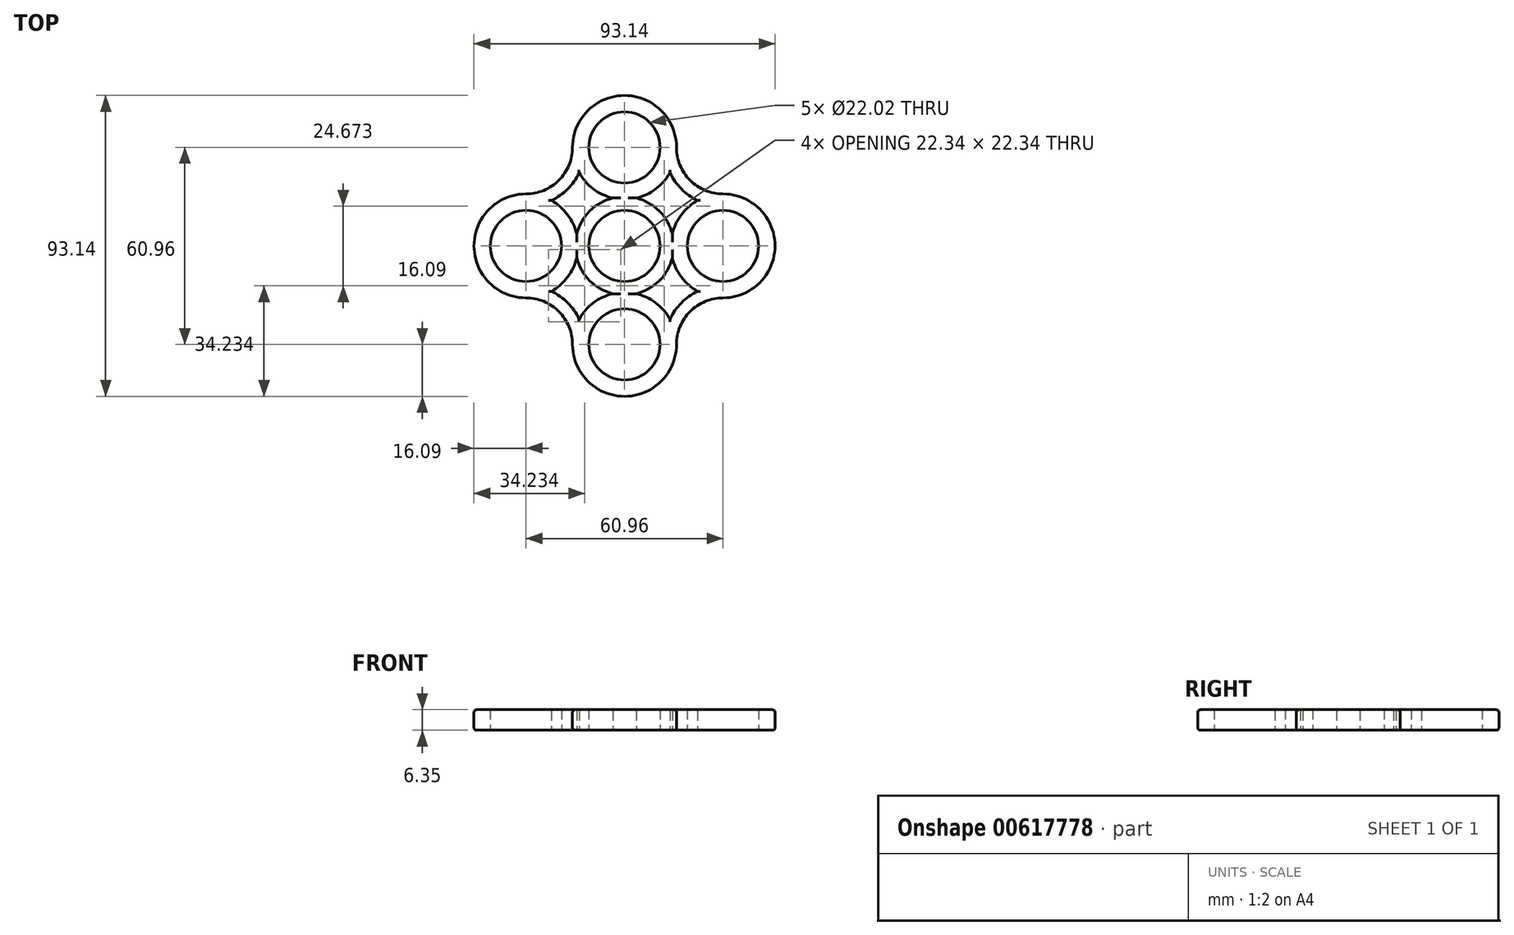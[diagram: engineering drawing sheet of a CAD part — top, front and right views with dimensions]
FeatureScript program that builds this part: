
annotation { "Feature Type Name" : "Feature", "Feature Type Description" : "" }
export const myFeature = defineFeature(function(context is Context, id is Id, definition is map)
    precondition{}
    {
        {
            var Q0;
            Q0=qCreatedBy(makeId("Top.planeOp"),FACE);
            var sketch = newSketch(context, id + "F0", { "sketchPlane" : qUnion([Q0])});
            skCircle(sketch, "E0", {"center": v(0, 0) * mm, "radius": 11.01 * mm});
            skLineSegment(sketch, "E1", {"start": v(0, 0) * mm, "end": v(-30.48, 0) * mm});
            skLineSegment(sketch, "E2", {"start": v(0, 0) * mm, "end": v(0, -30.48) * mm});
            skLineSegment(sketch, "E3", {"start": v(0, 0) * mm, "end": v(30.48, 0) * mm});
            skLineSegment(sketch, "E4", {"start": v(0, 0) * mm, "end": v(0, 30.48) * mm});
            skCircle(sketch, "E5", {"center": v(30.48, 0) * mm, "radius": 11.01 * mm});
            skCircle(sketch, "E6", {"center": v(-30.48, 0) * mm, "radius": 11.01 * mm});
            skCircle(sketch, "E7", {"center": v(0, 30.48) * mm, "radius": 11.01 * mm});
            skCircle(sketch, "E8", {"center": v(0, -30.48) * mm, "radius": 11.01 * mm});
            skCircle(sketch, "E9", {"center": v(-30.48, 0) * mm, "radius": 16.1 * mm});
            skCircle(sketch, "E10", {"center": v(0, 30.48) * mm, "radius": 16.1 * mm});
            skCircle(sketch, "E11", {"center": v(30.48, 0) * mm, "radius": 16.1 * mm});
            skCircle(sketch, "E12", {"center": v(0, -30.48) * mm, "radius": 16.1 * mm});
            skArc(sketch, "E13", {"start": v(-30.47, 16.1) * mm, "mid": v(-20.3, 20.3) * mm, "end": v(-16.1, 30.47) * mm});
            skArc(sketch, "E14", {"start": v(-16.1, -30.47) * mm, "mid": v(-20.3, -20.3) * mm, "end": v(-30.47, -16.1) * mm});
            skArc(sketch, "E15", {"start": v(30.47, -16.1) * mm, "mid": v(20.3, -20.3) * mm, "end": v(16.1, -30.47) * mm});
            skArc(sketch, "E16", {"start": v(16.1, 30.47) * mm, "mid": v(20.3, 20.3) * mm, "end": v(30.47, 16.1) * mm});
            skArc(sketch, "E17", {"start": v(-14.05, 22.64) * mm, "mid": v(-17.6, 17.6) * mm, "end": v(-22.64, 14.05) * mm});
            skArc(sketch, "E18", {"start": v(14.05, 22.64) * mm, "mid": v(17.6, 17.6) * mm, "end": v(22.64, 14.05) * mm});
            skArc(sketch, "E19", {"start": v(-22.64, -14.05) * mm, "mid": v(-17.6, -17.6) * mm, "end": v(-14.05, -22.64) * mm});
            skArc(sketch, "E20", {"start": v(14.05, -22.64) * mm, "mid": v(17.6, -17.6) * mm, "end": v(22.64, -14.05) * mm});
            skCircle(sketch, "E21", {"center": v(0, 0) * mm, "radius": 15.24 * mm});
            skSolve(sketch);
        }
        {
            var Q0;
            Q0 = qSketchRegion(id + "F0", true);
            var Q1;
            {var subQ0=sQuery(id+"F0.wireOp",EDGE,"E1");var subQ1=sQuery(id+"F0.wireOp",EDGE,"E0");var subQ2=makeQuery(id+"F0.imprint","INTERSECT",VERTEX,{"derivedFrom":[subQ1,subQ0]});Q1=makeQuery(id+"F0.imprint","IMPRINT",FACE,{"disambiguationData":[TD([[makeQuery(id+"F0.imprint","IMPRINT",EDGE,{"disambiguationData":[TD([[subQ2,-1.0]])],"derivedFrom":subQ1}),-1.0]])]});}
            var Q2;
            {var subQ0=sQuery(id+"F0.wireOp",EDGE,"E4");var subQ1=sQuery(id+"F0.wireOp",EDGE,"E0");var subQ2=makeQuery(id+"F0.imprint","INTERSECT",VERTEX,{"derivedFrom":[subQ1,subQ0]});Q2=makeQuery(id+"F0.imprint","IMPRINT",FACE,{"disambiguationData":[TD([[makeQuery(id+"F0.imprint","IMPRINT",EDGE,{"disambiguationData":[TD([[subQ2,-1.0]])],"derivedFrom":subQ1}),-1.0]])]});}
            var Q3;
            {var subQ0=sQuery(id+"F0.wireOp",EDGE,"E4");var subQ1=sQuery(id+"F0.wireOp",EDGE,"E0");var subQ2=makeQuery(id+"F0.imprint","INTERSECT",VERTEX,{"derivedFrom":[subQ1,subQ0]});Q3=makeQuery(id+"F0.imprint","IMPRINT",FACE,{"disambiguationData":[TD([[makeQuery(id+"F0.imprint","IMPRINT",EDGE,{"disambiguationData":[TD([[subQ2,1.0]])],"derivedFrom":subQ1}),-1.0]])]});}
            var Q4;
            {var subQ0=sQuery(id+"F0.wireOp",EDGE,"E3");var subQ1=sQuery(id+"F0.wireOp",EDGE,"E0");var subQ2=makeQuery(id+"F0.imprint","INTERSECT",VERTEX,{"derivedFrom":[subQ1,subQ0]});Q4=makeQuery(id+"F0.imprint","IMPRINT",FACE,{"disambiguationData":[TD([[makeQuery(id+"F0.imprint","IMPRINT",EDGE,{"disambiguationData":[TD([[subQ2,1.0]])],"derivedFrom":subQ1}),-1.0]])]});}
            var Q5;
            {var subQ0=sQuery(id+"F0.wireOp",EDGE,"E21");var subQ1=sQuery(id+"F0.wireOp",EDGE,"E1");var subQ2=makeQuery(id+"F0.imprint","INTERSECT",VERTEX,{"derivedFrom":[subQ1,subQ0]});Q5=makeQuery(id+"F0.imprint","IMPRINT",FACE,{"disambiguationData":[TD([[makeQuery(id+"F0.imprint","IMPRINT",EDGE,{"disambiguationData":[TD([[subQ2,1.0]])],"derivedFrom":subQ1}),-1.0]])]});}
            var Q6;
            {var subQ0=sQuery(id+"F0.wireOp",EDGE,"E21");var subQ1=sQuery(id+"F0.wireOp",EDGE,"E1");var subQ2=makeQuery(id+"F0.imprint","INTERSECT",VERTEX,{"derivedFrom":[subQ1,subQ0]});Q6=makeQuery(id+"F0.imprint","IMPRINT",FACE,{"disambiguationData":[TD([[makeQuery(id+"F0.imprint","IMPRINT",EDGE,{"disambiguationData":[TD([[subQ2,1.0]])],"derivedFrom":subQ1}),1.0]])]});}
            var Q7;
            {var subQ0=sQuery(id+"F0.wireOp",EDGE,"E21");var subQ1=sQuery(id+"F0.wireOp",EDGE,"E4");var subQ2=makeQuery(id+"F0.imprint","INTERSECT",VERTEX,{"derivedFrom":[subQ1,subQ0]});Q7=makeQuery(id+"F0.imprint","IMPRINT",FACE,{"disambiguationData":[TD([[makeQuery(id+"F0.imprint","IMPRINT",EDGE,{"disambiguationData":[TD([[subQ2,1.0]])],"derivedFrom":subQ1}),1.0]])]});}
            var Q8;
            {var subQ0=sQuery(id+"F0.wireOp",EDGE,"E21");var subQ1=sQuery(id+"F0.wireOp",EDGE,"E4");var subQ2=makeQuery(id+"F0.imprint","INTERSECT",VERTEX,{"derivedFrom":[subQ1,subQ0]});Q8=makeQuery(id+"F0.imprint","IMPRINT",FACE,{"disambiguationData":[TD([[makeQuery(id+"F0.imprint","IMPRINT",EDGE,{"disambiguationData":[TD([[subQ2,1.0]])],"derivedFrom":subQ1}),-1.0]])]});}
            var Q9;
            {var subQ0=sQuery(id+"F0.wireOp",EDGE,"E21");var subQ1=sQuery(id+"F0.wireOp",EDGE,"E3");var subQ2=makeQuery(id+"F0.imprint","INTERSECT",VERTEX,{"derivedFrom":[subQ1,subQ0]});Q9=makeQuery(id+"F0.imprint","IMPRINT",FACE,{"disambiguationData":[TD([[makeQuery(id+"F0.imprint","IMPRINT",EDGE,{"disambiguationData":[TD([[subQ2,1.0]])],"derivedFrom":subQ1}),1.0]])]});}
            var Q10;
            {var subQ0=sQuery(id+"F0.wireOp",EDGE,"E21");var subQ1=sQuery(id+"F0.wireOp",EDGE,"E3");var subQ2=makeQuery(id+"F0.imprint","INTERSECT",VERTEX,{"derivedFrom":[subQ1,subQ0]});Q10=makeQuery(id+"F0.imprint","IMPRINT",FACE,{"disambiguationData":[TD([[makeQuery(id+"F0.imprint","IMPRINT",EDGE,{"disambiguationData":[TD([[subQ2,1.0]])],"derivedFrom":subQ1}),-1.0]])]});}
            var Q11;
            {var subQ0=sQuery(id+"F0.wireOp",EDGE,"E21");var subQ1=sQuery(id+"F0.wireOp",EDGE,"E2");var subQ2=makeQuery(id+"F0.imprint","INTERSECT",VERTEX,{"derivedFrom":[subQ1,subQ0]});Q11=makeQuery(id+"F0.imprint","IMPRINT",FACE,{"disambiguationData":[TD([[makeQuery(id+"F0.imprint","IMPRINT",EDGE,{"disambiguationData":[TD([[subQ2,1.0]])],"derivedFrom":subQ1}),1.0]])]});}
            var Q12;
            {var subQ0=sQuery(id+"F0.wireOp",EDGE,"E21");var subQ1=sQuery(id+"F0.wireOp",EDGE,"E2");var subQ2=makeQuery(id+"F0.imprint","INTERSECT",VERTEX,{"derivedFrom":[subQ1,subQ0]});Q12=makeQuery(id+"F0.imprint","IMPRINT",FACE,{"disambiguationData":[TD([[makeQuery(id+"F0.imprint","IMPRINT",EDGE,{"disambiguationData":[TD([[subQ2,1.0]])],"derivedFrom":subQ1}),-1.0]])]});}
            var Q13;
            {var subQ0=sQuery(id+"F0.wireOp",EDGE,"ufLXqPXd-shLM-E6S0-tGkO-5ok8c0KJ1qn1");Q13=makeQuery(id+"F0.imprint","IMPRINT",FACE,{"disambiguationData":[TD([[makeQuery(id+"F0.imprint","IMPRINT",EDGE,{"derivedFrom":subQ0}),-1.0]])]});}
            var Q14;
            {var subQ0=sQuery(id+"F0.wireOp",EDGE,"inb3N0IN-n71V-Iyvo-hvQc-OrFp1SuvMqcb");Q14=makeQuery(id+"F0.imprint","IMPRINT",FACE,{"disambiguationData":[TD([[makeQuery(id+"F0.imprint","IMPRINT",EDGE,{"derivedFrom":subQ0}),-1.0]])]});}
            extrude(context, id + "F1", {"entities" : qUnion([Q0, Q1, Q2, Q3, Q4, Q5, Q6, Q7, Q8, Q9, Q10, Q11, Q12, Q13, Q14]), "depth" : 6.35 * mm, "offsetDistance" : 25.4 * mm});
        }
        {
            var Q0;
            {var subQ0=sQuery(id+"F0.wireOp",EDGE,"E11");Q0=makeQuery(id+"F1.opExtrude","CAP_EDGE",EDGE,{"disambiguationData":[OSD([subQ0]),TDD([makeQuery(id+"F0.imprint","IMPRINT",EDGE,{"disambiguationData":[TD([[makeQuery(id+"F0.imprint","INTERSECT",VERTEX,{"derivedFrom":[subQ0,sQuery(id+"F0.wireOp",EDGE,"E18")]}),-1.0]])],"derivedFrom":subQ0})])],"isStart":true});}
            var Q1;
            {var subQ0=sQuery(id+"F0.wireOp",EDGE,"E21");Q1=makeQuery(id+"F1.opExtrude","CAP_EDGE",EDGE,{"disambiguationData":[OSD([subQ0]),TDD([makeQuery(id+"F0.imprint","IMPRINT",EDGE,{"disambiguationData":[TD([[makeQuery(id+"F0.imprint","INTERSECT",VERTEX,{"disambiguationData":[OD(1.0)],"derivedFrom":[sQuery(id+"F0.wireOp",EDGE,"E10"),subQ0]}),1.0]])],"derivedFrom":subQ0})])],"isStart":true});}
            var Q2;
            {var subQ0=sQuery(id+"F0.wireOp",EDGE,"E10");Q2=makeQuery(id+"F1.opExtrude","CAP_EDGE",EDGE,{"disambiguationData":[OSD([subQ0]),TDD([makeQuery(id+"F0.imprint","IMPRINT",EDGE,{"disambiguationData":[TD([[makeQuery(id+"F0.imprint","INTERSECT",VERTEX,{"derivedFrom":[subQ0,sQuery(id+"F0.wireOp",EDGE,"E18")]}),1.0]])],"derivedFrom":subQ0})])],"isStart":true});}
            var Q3;
            Q3=makeQuery(id+"F1.opExtrude","CAP_EDGE",EDGE,{"disambiguationData":[OSD([sQuery(id+"F0.wireOp",EDGE,"E18")])],"isStart":true});
            var Q4;
            {var subQ0=sQuery(id+"F0.wireOp",EDGE,"E21");Q4=makeQuery(id+"F1.opExtrude","CAP_EDGE",EDGE,{"disambiguationData":[OSD([subQ0]),TDD([makeQuery(id+"F0.imprint","IMPRINT",EDGE,{"disambiguationData":[TD([[makeQuery(id+"F0.imprint","INTERSECT",VERTEX,{"disambiguationData":[OD(1.0)],"derivedFrom":[sQuery(id+"F0.wireOp",EDGE,"E11"),subQ0]}),1.0]])],"derivedFrom":subQ0})])],"isStart":true});}
            var Q5;
            {var subQ0=sQuery(id+"F0.wireOp",EDGE,"E11");Q5=makeQuery(id+"F1.opExtrude","CAP_EDGE",EDGE,{"disambiguationData":[OSD([subQ0]),TDD([makeQuery(id+"F0.imprint","IMPRINT",EDGE,{"disambiguationData":[TD([[makeQuery(id+"F0.imprint","INTERSECT",VERTEX,{"derivedFrom":[subQ0,sQuery(id+"F0.wireOp",EDGE,"E20")]}),1.0]])],"derivedFrom":subQ0})])],"isStart":true});}
            var Q6;
            Q6=makeQuery(id+"F1.opExtrude","CAP_EDGE",EDGE,{"disambiguationData":[OSD([sQuery(id+"F0.wireOp",EDGE,"E20")])],"isStart":true});
            var Q7;
            {var subQ0=sQuery(id+"F0.wireOp",EDGE,"E12");Q7=makeQuery(id+"F1.opExtrude","CAP_EDGE",EDGE,{"disambiguationData":[OSD([subQ0]),TDD([makeQuery(id+"F0.imprint","IMPRINT",EDGE,{"disambiguationData":[TD([[makeQuery(id+"F0.imprint","INTERSECT",VERTEX,{"derivedFrom":[subQ0,sQuery(id+"F0.wireOp",EDGE,"E20")]}),-1.0]])],"derivedFrom":subQ0})])],"isStart":true});}
            var Q8;
            {var subQ0=sQuery(id+"F0.wireOp",EDGE,"E12");Q8=makeQuery(id+"F1.opExtrude","CAP_EDGE",EDGE,{"disambiguationData":[OSD([subQ0]),TDD([makeQuery(id+"F0.imprint","IMPRINT",EDGE,{"disambiguationData":[TD([[makeQuery(id+"F0.imprint","INTERSECT",VERTEX,{"derivedFrom":[subQ0,sQuery(id+"F0.wireOp",EDGE,"E19")]}),1.0]])],"derivedFrom":subQ0})])],"isStart":true});}
            var Q9;
            {var subQ0=sQuery(id+"F0.wireOp",EDGE,"E21");Q9=makeQuery(id+"F1.opExtrude","CAP_EDGE",EDGE,{"disambiguationData":[OSD([subQ0]),TDD([makeQuery(id+"F0.imprint","IMPRINT",EDGE,{"disambiguationData":[TD([[makeQuery(id+"F0.imprint","INTERSECT",VERTEX,{"disambiguationData":[OD(1.0)],"derivedFrom":[sQuery(id+"F0.wireOp",EDGE,"E9"),subQ0]}),-1.0]])],"derivedFrom":subQ0})])],"isStart":true});}
            var Q10;
            {var subQ0=sQuery(id+"F0.wireOp",EDGE,"E9");Q10=makeQuery(id+"F1.opExtrude","CAP_EDGE",EDGE,{"disambiguationData":[OSD([subQ0]),TDD([makeQuery(id+"F0.imprint","IMPRINT",EDGE,{"disambiguationData":[TD([[makeQuery(id+"F0.imprint","INTERSECT",VERTEX,{"derivedFrom":[subQ0,sQuery(id+"F0.wireOp",EDGE,"E19")]}),-1.0]])],"derivedFrom":subQ0})])],"isStart":true});}
            var Q11;
            Q11=makeQuery(id+"F1.opExtrude","CAP_EDGE",EDGE,{"disambiguationData":[OSD([sQuery(id+"F0.wireOp",EDGE,"E19")])],"isStart":true});
            var Q12;
            Q12=makeQuery(id+"F1.opExtrude","CAP_EDGE",EDGE,{"disambiguationData":[OSD([sQuery(id+"F0.wireOp",EDGE,"E17")])],"isStart":true});
            var Q13;
            {var subQ0=sQuery(id+"F0.wireOp",EDGE,"E10");Q13=makeQuery(id+"F1.opExtrude","CAP_EDGE",EDGE,{"disambiguationData":[OSD([subQ0]),TDD([makeQuery(id+"F0.imprint","IMPRINT",EDGE,{"disambiguationData":[TD([[makeQuery(id+"F0.imprint","INTERSECT",VERTEX,{"derivedFrom":[subQ0,sQuery(id+"F0.wireOp",EDGE,"E17")]}),-1.0]])],"derivedFrom":subQ0})])],"isStart":true});}
            var Q14;
            {var subQ0=sQuery(id+"F0.wireOp",EDGE,"E21");Q14=makeQuery(id+"F1.opExtrude","CAP_EDGE",EDGE,{"disambiguationData":[OSD([subQ0]),TDD([makeQuery(id+"F0.imprint","IMPRINT",EDGE,{"disambiguationData":[TD([[makeQuery(id+"F0.imprint","INTERSECT",VERTEX,{"disambiguationData":[OD(0.0)],"derivedFrom":[sQuery(id+"F0.wireOp",EDGE,"E9"),subQ0]}),1.0]])],"derivedFrom":subQ0})])],"isStart":true});}
            var Q15;
            {var subQ0=sQuery(id+"F0.wireOp",EDGE,"E9");Q15=makeQuery(id+"F1.opExtrude","CAP_EDGE",EDGE,{"disambiguationData":[OSD([subQ0]),TDD([makeQuery(id+"F0.imprint","IMPRINT",EDGE,{"disambiguationData":[TD([[makeQuery(id+"F0.imprint","INTERSECT",VERTEX,{"derivedFrom":[subQ0,sQuery(id+"F0.wireOp",EDGE,"E17")]}),1.0]])],"derivedFrom":subQ0})])],"isStart":true});}
            var Q16;
            {var subQ0=sQuery(id+"F0.wireOp",EDGE,"E10");Q16=makeQuery(id+"F1.opExtrude","CAP_EDGE",EDGE,{"disambiguationData":[OSD([subQ0]),TDD([makeQuery(id+"F0.imprint","IMPRINT",EDGE,{"disambiguationData":[TD([[makeQuery(id+"F0.imprint","INTERSECT",VERTEX,{"derivedFrom":[subQ0,sQuery(id+"F0.wireOp",EDGE,"E18")]}),1.0]])],"derivedFrom":subQ0})])],"isStart":false});}
            var Q17;
            Q17=makeQuery(id+"F1.opExtrude","CAP_EDGE",EDGE,{"disambiguationData":[OSD([sQuery(id+"F0.wireOp",EDGE,"E18")])],"isStart":false});
            var Q18;
            {var subQ0=sQuery(id+"F0.wireOp",EDGE,"E11");Q18=makeQuery(id+"F1.opExtrude","CAP_EDGE",EDGE,{"disambiguationData":[OSD([subQ0]),TDD([makeQuery(id+"F0.imprint","IMPRINT",EDGE,{"disambiguationData":[TD([[makeQuery(id+"F0.imprint","INTERSECT",VERTEX,{"derivedFrom":[subQ0,sQuery(id+"F0.wireOp",EDGE,"E18")]}),-1.0]])],"derivedFrom":subQ0})])],"isStart":false});}
            var Q19;
            {var subQ0=sQuery(id+"F0.wireOp",EDGE,"E21");Q19=makeQuery(id+"F1.opExtrude","CAP_EDGE",EDGE,{"disambiguationData":[OSD([subQ0]),TDD([makeQuery(id+"F0.imprint","IMPRINT",EDGE,{"disambiguationData":[TD([[makeQuery(id+"F0.imprint","INTERSECT",VERTEX,{"disambiguationData":[OD(1.0)],"derivedFrom":[sQuery(id+"F0.wireOp",EDGE,"E10"),subQ0]}),1.0]])],"derivedFrom":subQ0})])],"isStart":false});}
            var Q20;
            {var subQ0=sQuery(id+"F0.wireOp",EDGE,"E10");Q20=makeQuery(id+"F1.opExtrude","CAP_EDGE",EDGE,{"disambiguationData":[OSD([subQ0]),TDD([makeQuery(id+"F0.imprint","IMPRINT",EDGE,{"disambiguationData":[TD([[makeQuery(id+"F0.imprint","INTERSECT",VERTEX,{"derivedFrom":[subQ0,sQuery(id+"F0.wireOp",EDGE,"E17")]}),-1.0]])],"derivedFrom":subQ0})])],"isStart":false});}
            var Q21;
            Q21=makeQuery(id+"F1.opExtrude","CAP_EDGE",EDGE,{"disambiguationData":[OSD([sQuery(id+"F0.wireOp",EDGE,"E17")])],"isStart":false});
            var Q22;
            {var subQ0=sQuery(id+"F0.wireOp",EDGE,"E21");Q22=makeQuery(id+"F1.opExtrude","CAP_EDGE",EDGE,{"disambiguationData":[OSD([subQ0]),TDD([makeQuery(id+"F0.imprint","IMPRINT",EDGE,{"disambiguationData":[TD([[makeQuery(id+"F0.imprint","INTERSECT",VERTEX,{"disambiguationData":[OD(0.0)],"derivedFrom":[sQuery(id+"F0.wireOp",EDGE,"E9"),subQ0]}),1.0]])],"derivedFrom":subQ0})])],"isStart":false});}
            var Q23;
            {var subQ0=sQuery(id+"F0.wireOp",EDGE,"E9");Q23=makeQuery(id+"F1.opExtrude","CAP_EDGE",EDGE,{"disambiguationData":[OSD([subQ0]),TDD([makeQuery(id+"F0.imprint","IMPRINT",EDGE,{"disambiguationData":[TD([[makeQuery(id+"F0.imprint","INTERSECT",VERTEX,{"derivedFrom":[subQ0,sQuery(id+"F0.wireOp",EDGE,"E17")]}),1.0]])],"derivedFrom":subQ0})])],"isStart":false});}
            var Q24;
            {var subQ0=sQuery(id+"F0.wireOp",EDGE,"E9");Q24=makeQuery(id+"F1.opExtrude","CAP_EDGE",EDGE,{"disambiguationData":[OSD([subQ0]),TDD([makeQuery(id+"F0.imprint","IMPRINT",EDGE,{"disambiguationData":[TD([[makeQuery(id+"F0.imprint","INTERSECT",VERTEX,{"derivedFrom":[subQ0,sQuery(id+"F0.wireOp",EDGE,"E19")]}),-1.0]])],"derivedFrom":subQ0})])],"isStart":false});}
            var Q25;
            {var subQ0=sQuery(id+"F0.wireOp",EDGE,"E21");Q25=makeQuery(id+"F1.opExtrude","CAP_EDGE",EDGE,{"disambiguationData":[OSD([subQ0]),TDD([makeQuery(id+"F0.imprint","IMPRINT",EDGE,{"disambiguationData":[TD([[makeQuery(id+"F0.imprint","INTERSECT",VERTEX,{"disambiguationData":[OD(1.0)],"derivedFrom":[sQuery(id+"F0.wireOp",EDGE,"E9"),subQ0]}),-1.0]])],"derivedFrom":subQ0})])],"isStart":false});}
            var Q26;
            Q26=makeQuery(id+"F1.opExtrude","CAP_EDGE",EDGE,{"disambiguationData":[OSD([sQuery(id+"F0.wireOp",EDGE,"E19")])],"isStart":false});
            var Q27;
            {var subQ0=sQuery(id+"F0.wireOp",EDGE,"E12");Q27=makeQuery(id+"F1.opExtrude","CAP_EDGE",EDGE,{"disambiguationData":[OSD([subQ0]),TDD([makeQuery(id+"F0.imprint","IMPRINT",EDGE,{"disambiguationData":[TD([[makeQuery(id+"F0.imprint","INTERSECT",VERTEX,{"derivedFrom":[subQ0,sQuery(id+"F0.wireOp",EDGE,"E19")]}),1.0]])],"derivedFrom":subQ0})])],"isStart":false});}
            var Q28;
            {var subQ0=sQuery(id+"F0.wireOp",EDGE,"E12");Q28=makeQuery(id+"F1.opExtrude","CAP_EDGE",EDGE,{"disambiguationData":[OSD([subQ0]),TDD([makeQuery(id+"F0.imprint","IMPRINT",EDGE,{"disambiguationData":[TD([[makeQuery(id+"F0.imprint","INTERSECT",VERTEX,{"derivedFrom":[subQ0,sQuery(id+"F0.wireOp",EDGE,"E20")]}),-1.0]])],"derivedFrom":subQ0})])],"isStart":false});}
            var Q29;
            {var subQ0=sQuery(id+"F0.wireOp",EDGE,"E21");Q29=makeQuery(id+"F1.opExtrude","CAP_EDGE",EDGE,{"disambiguationData":[OSD([subQ0]),TDD([makeQuery(id+"F0.imprint","IMPRINT",EDGE,{"disambiguationData":[TD([[makeQuery(id+"F0.imprint","INTERSECT",VERTEX,{"disambiguationData":[OD(1.0)],"derivedFrom":[sQuery(id+"F0.wireOp",EDGE,"E11"),subQ0]}),1.0]])],"derivedFrom":subQ0})])],"isStart":false});}
            var Q30;
            {var subQ0=sQuery(id+"F0.wireOp",EDGE,"E11");Q30=makeQuery(id+"F1.opExtrude","CAP_EDGE",EDGE,{"disambiguationData":[OSD([subQ0]),TDD([makeQuery(id+"F0.imprint","IMPRINT",EDGE,{"disambiguationData":[TD([[makeQuery(id+"F0.imprint","INTERSECT",VERTEX,{"derivedFrom":[subQ0,sQuery(id+"F0.wireOp",EDGE,"E20")]}),1.0]])],"derivedFrom":subQ0})])],"isStart":false});}
            var Q31;
            Q31=makeQuery(id+"F1.opExtrude","CAP_EDGE",EDGE,{"disambiguationData":[OSD([sQuery(id+"F0.wireOp",EDGE,"E20")])],"isStart":false});
            fillet(context, id + "F2", {"entities" : qUnion([Q0, Q1, Q2, Q3, Q4, Q5, Q6, Q7, Q8, Q9, Q10, Q11, Q12, Q13, Q14, Q15, Q16, Q17, Q18, Q19, Q20, Q21, Q22, Q23, Q24, Q25, Q26, Q27, Q28, Q29, Q30, Q31]), "radius" : 0.38 * mm, "tangentPropagation" : true, "allowEdgeOverflow" : false});
        }
        {
            var Q0;
            {var subQ0=sQuery(id+"F0.wireOp",EDGE,"E10");Q0=makeQuery(id+"F1.opExtrude","CAP_EDGE",EDGE,{"disambiguationData":[OSD([subQ0]),TDD([makeQuery(id+"F0.imprint","IMPRINT",EDGE,{"disambiguationData":[TD([[makeQuery(id+"F0.imprint","INTERSECT",VERTEX,{"derivedFrom":[subQ0,sQuery(id+"F0.wireOp",EDGE,"E13")]}),1.0]])],"derivedFrom":subQ0})])],"isStart":true});}
            var Q1;
            {var subQ0=sQuery(id+"F0.wireOp",EDGE,"E10");Q1=makeQuery(id+"F1.opExtrude","CAP_EDGE",EDGE,{"disambiguationData":[OSD([subQ0]),TDD([makeQuery(id+"F0.imprint","IMPRINT",EDGE,{"disambiguationData":[TD([[makeQuery(id+"F0.imprint","INTERSECT",VERTEX,{"derivedFrom":[subQ0,sQuery(id+"F0.wireOp",EDGE,"E13")]}),1.0]])],"derivedFrom":subQ0})])],"isStart":false});}
            fillet(context, id + "F3", {"entities" : qUnion([Q0, Q1]), "radius" : 0.76 * mm, "tangentPropagation" : true, "allowEdgeOverflow" : false});
        }
    });
